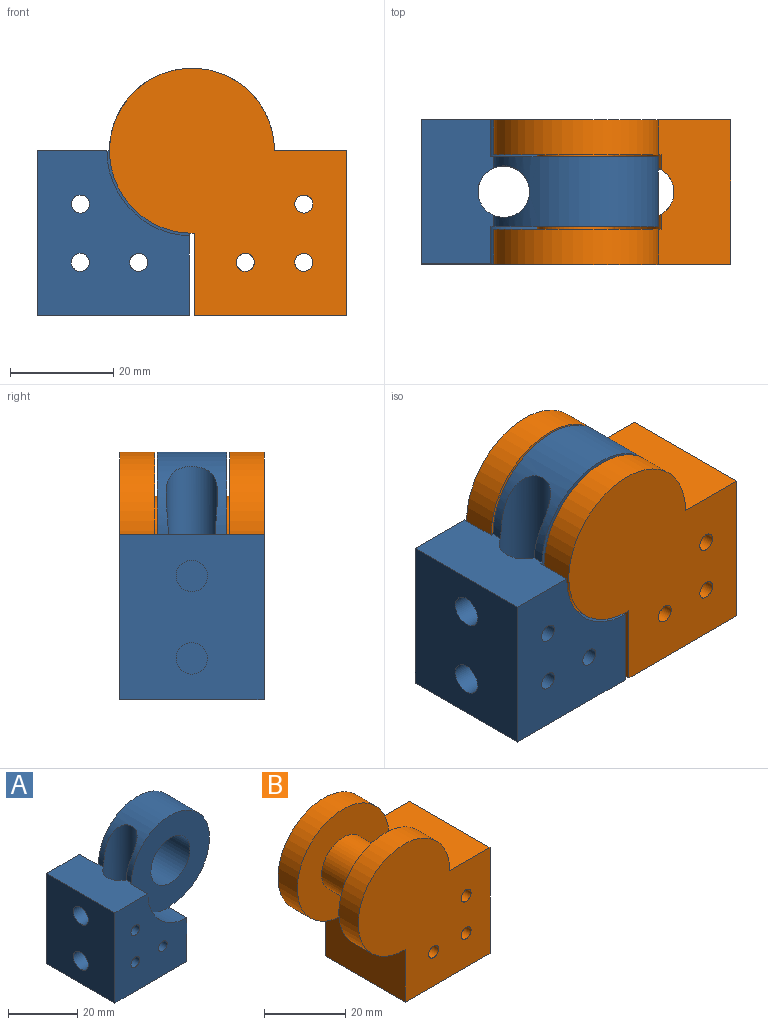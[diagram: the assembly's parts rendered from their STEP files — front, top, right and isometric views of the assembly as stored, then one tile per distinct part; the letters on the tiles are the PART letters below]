
ASSEMBLY  parts=2 mates=1
PART A: 21 faces, bbox 46x28x48 mm
  f0: cylinder r=16mm len=32mm, axis (0,1,0), area 879.7mm2, adj f2,f3,f5,f11,f20
  f1: cylinder r=1.75mm len=28mm, axis (0,-1,0), area 247.4mm2, adj f4,f6,f20
  f2: plane 32.52x32.52mm, normal (0,-1,0), area 615.8mm2, adj f0,f5,f10,f11,f12,f13
  f3: plane 32.52x32.52mm, normal (0,1,0), area 615.8mm2, adj f0,f5,f9,f11,f12,f13
  f4: plane 32.02x29.53mm, normal (0,-1,0), area 709.4mm2, adj f1,f5,f7,f8,f10,f12,f14,f15
  f5: plane 28x14mm, normal (0,0,1), area 364.9mm2, adj f0,f2,f3,f4,f6,f7,f9,f10
  f6: plane 32.02x29.64mm, normal (0,1,0), area 709.4mm2, adj f1,f5,f7,f8,f9,f12,f14,f15
  f7: plane 32x28mm, normal (-1,0,0), area 837.6mm2, adj f4,f5,f6,f8,f16,f18
  f8: plane 29.5x28mm, normal (0,0,-1), area 747.5mm2, adj f4,f6,f7,f12,f20
  f9: cylinder r=16.5mm len=16.49mm, axis (0,-1,0), area 184.3mm2, adj f3,f5,f6,f12
  f10: cylinder r=16.5mm len=16.49mm, axis (0,1,0), area 184.3mm2, adj f2,f4,f5,f12
  f11: plane 13.5x0.5mm, normal (0,0,-1), area 6.7mm2, adj f0,f2,f3,f12
  f12: plane 28.02x16.02mm, normal (1,0,0), area 440.8mm2, adj f2,f3,f4,f6,f8,f9,f10,f11
  f13: cylinder r=8mm len=16mm, axis (0,-1,0), area 678.6mm2, adj f2,f3
  f14: cylinder r=1.75mm len=28mm, axis (0,-1,0), area 307.9mm2, adj f4,f6
  f15: cylinder r=1.75mm len=28mm, axis (0,-1,0), area 307.9mm2, adj f4,f6
  f16: cylinder r=3.05mm len=6.1mm, axis (-1,0,0), area 95.8mm2, adj f7,f17
  f17: plane 6.1x6.1mm, normal (-1,0,0), area 29.2mm2, adj f16
  f18: cylinder r=3.05mm len=6.1mm, axis (-1,0,0), area 95.8mm2, adj f7,f19
  f19: plane 6.1x6.1mm, normal (-1,0,0), area 29.2mm2, adj f18
  f20: cylinder r=5mm len=45.23mm, axis (0,0,-1), area 1174.9mm2, adj f0,f1,f5,f8
PART B: 18 faces, bbox 46x28x48 mm
  f0: cylinder r=16.5mm len=16.49mm, axis (0,-1,0), area 224.7mm2, adj f4,f8,f9,f13,f17
  f1: cylinder r=1.75mm len=28mm, axis (0,-1,0), area 247.3mm2, adj f3,f5,f17
  f2: plane 29.5x28mm, normal (0,0,-1), area 747.5mm2, adj f3,f5,f6,f13,f17
  f3: plane 48x46mm, normal (0,1,0), area 1526.3mm2, adj f1,f2,f4,f6,f10,f12,f13,f15
  f4: plane 28x14mm, normal (0,0,1), area 369.4mm2, adj f0,f3,f5,f6,f7,f8,f9,f10
  f5: plane 48x46mm, normal (0,-1,0), area 1526.3mm2, adj f1,f2,f4,f6,f7,f11,f13,f15
  f6: plane 32x28mm, normal (1,0,0), area 896mm2, adj f2,f3,f4,f5
  f7: cylinder r=16mm len=32mm, axis (0,1,0), area 508.9mm2, adj f4,f5,f8,f11
  f8: plane 32.52x32.52mm, normal (0,1,0), area 639.9mm2, adj f0,f4,f7,f11,f13,f14
  f9: plane 32.52x32.52mm, normal (0,-1,0), area 640mm2, adj f0,f4,f10,f12,f13,f14
  f10: cylinder r=16mm len=32mm, axis (0,-1,0), area 508.9mm2, adj f3,f4,f9,f12
  f11: plane 6.75x0.5mm, normal (0,0,-1), area 3.4mm2, adj f5,f7,f8,f13
  f12: plane 6.75x0.5mm, normal (0,0,-1), area 3.4mm2, adj f3,f9,f10,f13
  f13: plane 28.02x16.02mm, normal (-1,0,0), area 440.8mm2, adj f0,f2,f3,f5,f8,f9,f11,f12
  f14: cylinder r=7.5mm len=15mm, axis (0,1,0), area 683.3mm2, adj f8,f9
  f15: cylinder r=1.75mm len=28mm, axis (0,-1,0), area 307.9mm2, adj f3,f5
  f16: cylinder r=1.75mm len=28mm, axis (0,-1,0), area 307.9mm2, adj f3,f5
  f17: cylinder r=5mm len=32mm, axis (0,0,-1), area 782mm2, adj f0,f1,f2,f4
PLACE A t=(29.72,34.68,-2.48)mm
PLACE B t=(29.72,34.61,-2.48)mm
MATE cylindrical B.f0 <-> A.f0  axis (0,1,0) through (29.72,34.61,29.52)mm
